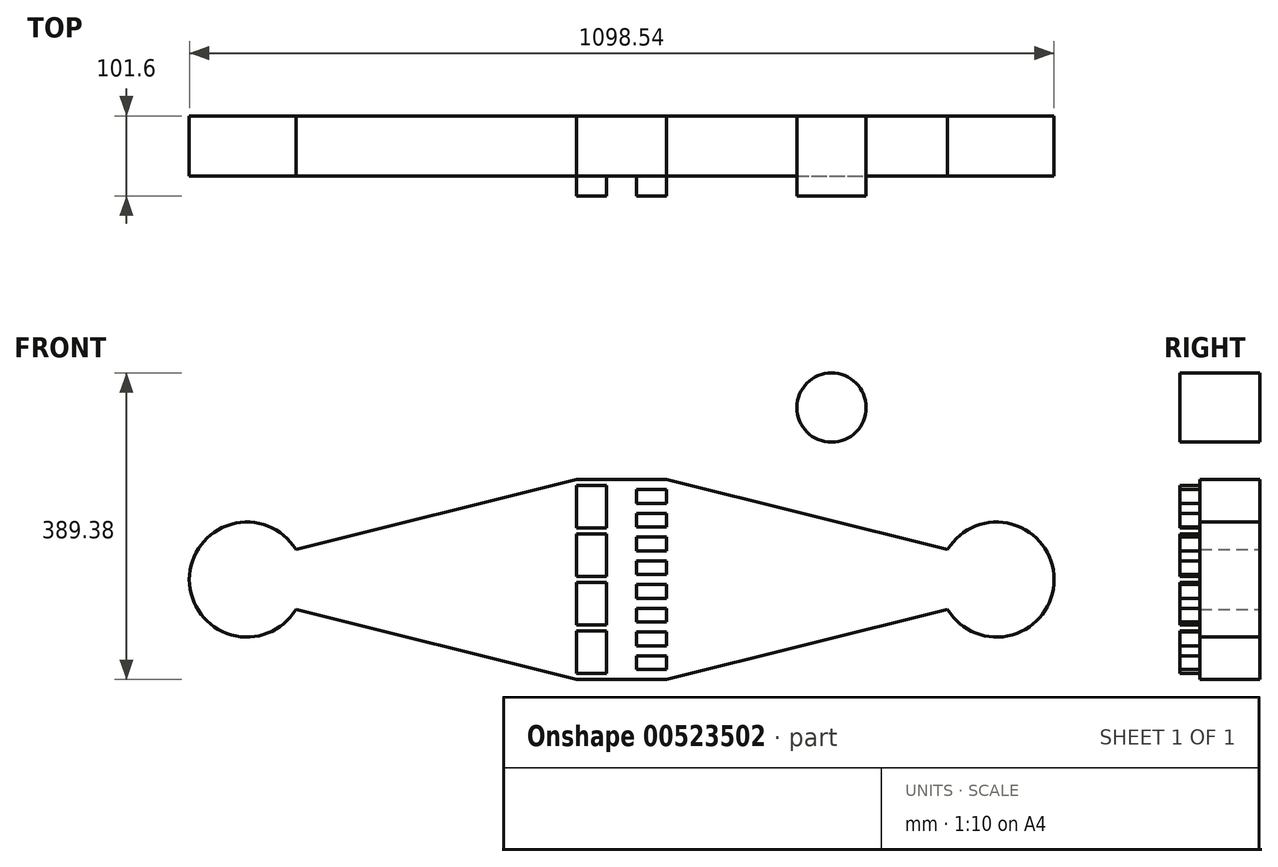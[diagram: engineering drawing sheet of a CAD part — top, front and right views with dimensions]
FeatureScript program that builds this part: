
annotation { "Feature Type Name" : "Feature", "Feature Type Description" : "" }
export const myFeature = defineFeature(function(context is Context, id is Id, definition is map)
    precondition{}
    {
        {
            var Q0;
            Q0=qCreatedBy(makeId("Front.planeOp"),FACE);
            var sketch = newSketch(context, id + "F0", { "sketchPlane" : qUnion([Q0])});
            skCircle(sketch, "E0", {"center": v(266.5, 218.44) * mm, "radius": 43.94 * mm});
            skCircle(sketch, "E1", {"center": v(266.5, -218.44) * mm, "radius": 43.94 * mm});
            skArc(sketch, "E2", {"start": v(-413.95, 38.1) * mm, "mid": v(-549.28, 0) * mm, "end": v(-413.95, -38.1) * mm});
            skArc(sketch, "E3", {"start": v(413.95, -38.1) * mm, "mid": v(549.28, 0) * mm, "end": v(413.95, 38.1) * mm});
            skLineSegment(sketch, "E4", {"start": v(-413.95, 38.1) * mm, "end": v(-57.53, 127) * mm});
            skLineSegment(sketch, "E5", {"start": v(-413.95, -38.1) * mm, "end": v(-57.53, -127) * mm});
            skLineSegment(sketch, "E6", {"start": v(56.77, 127) * mm, "end": v(413.95, 38.1) * mm});
            skLineSegment(sketch, "E7", {"start": v(56.77, -127) * mm, "end": v(413.95, -38.1) * mm});
            skLineSegment(sketch, "E8", {"start": v(-57.53, 127) * mm, "end": v(56.77, 127) * mm});
            skLineSegment(sketch, "E9", {"start": v(-57.53, -127) * mm, "end": v(56.77, -127) * mm});
            skCircle(sketch, "E10", {"center": v(-305.37, 218.44) * mm, "radius": 43.94 * mm});
            skCircle(sketch, "E11", {"center": v(-305.37, -218.44) * mm, "radius": 43.94 * mm});
            skLineSegment(sketch, "E12", {"start": v(-637.54, -320.04) * mm, "end": v(637.54, -320.04) * mm});
            skLineSegment(sketch, "E13", {"start": v(637.54, 320.04) * mm, "end": v(637.54, -320.04) * mm});
            skLineSegment(sketch, "E14", {"start": v(-637.54, 320.04) * mm, "end": v(-637.54, -320.04) * mm});
            skLineSegment(sketch, "E15", {"start": v(-57.53, 65.4) * mm, "end": v(-57.53, 119.38) * mm});
            skLineSegment(sketch, "E16", {"start": v(-57.53, 119.38) * mm, "end": v(-19.43, 119.38) * mm});
            skLineSegment(sketch, "E17", {"start": v(-19.43, 119.38) * mm, "end": v(-19.43, 65.4) * mm});
            skLineSegment(sketch, "E18", {"start": v(-19.43, 65.4) * mm, "end": v(-57.53, 65.4) * mm});
            skLineSegment(sketch, "E19", {"start": v(-57.53, 3.81) * mm, "end": v(-57.53, 57.79) * mm});
            skLineSegment(sketch, "E20", {"start": v(-57.53, 57.79) * mm, "end": v(-19.43, 57.79) * mm});
            skLineSegment(sketch, "E21", {"start": v(-19.43, 57.79) * mm, "end": v(-19.43, 3.81) * mm});
            skLineSegment(sketch, "E22", {"start": v(-19.43, 3.81) * mm, "end": v(-57.53, 3.81) * mm});
            skLineSegment(sketch, "E23", {"start": v(-57.53, -57.79) * mm, "end": v(-57.53, -3.81) * mm});
            skLineSegment(sketch, "E24", {"start": v(-57.53, -3.81) * mm, "end": v(-19.43, -3.81) * mm});
            skLineSegment(sketch, "E25", {"start": v(-19.43, -3.81) * mm, "end": v(-19.43, -57.79) * mm});
            skLineSegment(sketch, "E26", {"start": v(-19.43, -57.79) * mm, "end": v(-57.53, -57.79) * mm});
            skLineSegment(sketch, "E27", {"start": v(-57.53, -119.38) * mm, "end": v(-57.53, -65.4) * mm});
            skLineSegment(sketch, "E28", {"start": v(-57.53, -65.4) * mm, "end": v(-19.43, -65.4) * mm});
            skLineSegment(sketch, "E29", {"start": v(-19.43, -65.4) * mm, "end": v(-19.43, -119.38) * mm});
            skLineSegment(sketch, "E30", {"start": v(-19.43, -119.38) * mm, "end": v(-57.53, -119.38) * mm});
            skLineSegment(sketch, "E31", {"start": v(18.67, 96.84) * mm, "end": v(18.67, 114.3) * mm});
            skLineSegment(sketch, "E32", {"start": v(18.67, 114.3) * mm, "end": v(56.77, 114.3) * mm});
            skLineSegment(sketch, "E33", {"start": v(56.77, 114.3) * mm, "end": v(56.77, 96.84) * mm});
            skLineSegment(sketch, "E34", {"start": v(56.77, 96.84) * mm, "end": v(18.67, 96.84) * mm});
            skLineSegment(sketch, "E35", {"start": v(18.67, 66.68) * mm, "end": v(18.67, 84.14) * mm});
            skLineSegment(sketch, "E36", {"start": v(18.67, 84.14) * mm, "end": v(56.77, 84.14) * mm});
            skLineSegment(sketch, "E37", {"start": v(56.77, 84.14) * mm, "end": v(56.77, 66.68) * mm});
            skLineSegment(sketch, "E38", {"start": v(56.77, 66.68) * mm, "end": v(18.67, 66.68) * mm});
            skLineSegment(sketch, "E39", {"start": v(18.67, 36.51) * mm, "end": v(18.67, 53.98) * mm});
            skLineSegment(sketch, "E40", {"start": v(18.67, 53.98) * mm, "end": v(56.77, 53.98) * mm});
            skLineSegment(sketch, "E41", {"start": v(56.77, 53.98) * mm, "end": v(56.77, 36.51) * mm});
            skLineSegment(sketch, "E42", {"start": v(56.77, 36.51) * mm, "end": v(18.67, 36.51) * mm});
            skLineSegment(sketch, "E43", {"start": v(18.67, 6.35) * mm, "end": v(18.67, 23.81) * mm});
            skLineSegment(sketch, "E44", {"start": v(18.67, 23.81) * mm, "end": v(56.77, 23.81) * mm});
            skLineSegment(sketch, "E45", {"start": v(56.77, 23.81) * mm, "end": v(56.77, 6.35) * mm});
            skLineSegment(sketch, "E46", {"start": v(56.77, 6.35) * mm, "end": v(18.67, 6.35) * mm});
            skLineSegment(sketch, "E47", {"start": v(18.67, -23.81) * mm, "end": v(18.67, -6.35) * mm});
            skLineSegment(sketch, "E48", {"start": v(18.67, -6.35) * mm, "end": v(56.77, -6.35) * mm});
            skLineSegment(sketch, "E49", {"start": v(56.77, -6.35) * mm, "end": v(56.77, -23.81) * mm});
            skLineSegment(sketch, "E50", {"start": v(56.77, -23.81) * mm, "end": v(18.67, -23.81) * mm});
            skLineSegment(sketch, "E51", {"start": v(18.67, -53.98) * mm, "end": v(18.67, -36.51) * mm});
            skLineSegment(sketch, "E52", {"start": v(18.67, -36.51) * mm, "end": v(56.77, -36.51) * mm});
            skLineSegment(sketch, "E53", {"start": v(56.77, -36.51) * mm, "end": v(56.77, -53.98) * mm});
            skLineSegment(sketch, "E54", {"start": v(56.77, -53.98) * mm, "end": v(18.67, -53.98) * mm});
            skLineSegment(sketch, "E55", {"start": v(18.67, -84.14) * mm, "end": v(18.67, -66.68) * mm});
            skLineSegment(sketch, "E56", {"start": v(18.67, -66.68) * mm, "end": v(56.77, -66.68) * mm});
            skLineSegment(sketch, "E57", {"start": v(56.77, -66.68) * mm, "end": v(56.77, -84.14) * mm});
            skLineSegment(sketch, "E58", {"start": v(56.77, -84.14) * mm, "end": v(18.67, -84.14) * mm});
            skLineSegment(sketch, "E59", {"start": v(18.67, -114.3) * mm, "end": v(18.67, -96.84) * mm});
            skLineSegment(sketch, "E60", {"start": v(18.67, -96.84) * mm, "end": v(56.77, -96.84) * mm});
            skLineSegment(sketch, "E61", {"start": v(56.77, -96.84) * mm, "end": v(56.77, -114.3) * mm});
            skLineSegment(sketch, "E62", {"start": v(56.77, -114.3) * mm, "end": v(18.67, -114.3) * mm});
            skLineSegment(sketch, "E63", {"start": v(-637.54, 320.04) * mm, "end": v(637.54, 320.04) * mm});
            skLineSegment(sketch, "E64", {"start": v(637.54, -320.04) * mm, "end": v(-637.54, -320.04) * mm});
            skLineSegment(sketch, "E65", {"start": v(637.54, 320.04) * mm, "end": v(-637.54, 320.04) * mm});
            skSolve(sketch);
        }
        {
            var Q0;
            Q0=makeQuery(id+"F0.imprint","IMPRINT",FACE,{"disambiguationData":[TD([[makeQuery(id+"F0.imprint","IMPRINT",EDGE,{"derivedFrom":sQuery(id+"F0.wireOp",EDGE,"E0")}),1.0]])]});
            extrude(context, id + "F1", {"entities" : qUnion([Q0]), "depth" : 101.6 * mm, "offsetDistance" : 25.4 * mm});
        }
        {
            var Q0;
            Q0=makeQuery(id+"F0.imprint","IMPRINT",FACE,{"disambiguationData":[TD([[makeQuery(id+"F0.imprint","IMPRINT",EDGE,{"derivedFrom":sQuery(id+"F0.wireOp",EDGE,"E2")}),1.0]])]});
            extrude(context, id + "F2", {"entities" : qUnion([Q0]), "operationType" : NewBodyOperationType.ADD, "depth" : 76.2 * mm, "offsetDistance" : 25.4 * mm});
        }
        {
            var Q0;
            Q0=makeQuery(id+"F0.imprint","IMPRINT",FACE,{"disambiguationData":[TD([[makeQuery(id+"F0.imprint","IMPRINT",EDGE,{"derivedFrom":sQuery(id+"F0.wireOp",EDGE,"E19")}),-1.0]])]});
            var Q1;
            Q1=makeQuery(id+"F0.imprint","IMPRINT",FACE,{"disambiguationData":[TD([[makeQuery(id+"F0.imprint","IMPRINT",EDGE,{"derivedFrom":sQuery(id+"F0.wireOp",EDGE,"E23")}),-1.0]])]});
            var Q2;
            Q2=makeQuery(id+"F0.imprint","IMPRINT",FACE,{"disambiguationData":[TD([[makeQuery(id+"F0.imprint","IMPRINT",EDGE,{"derivedFrom":sQuery(id+"F0.wireOp",EDGE,"E27")}),-1.0]])]});
            var Q3;
            Q3=makeQuery(id+"F0.imprint","IMPRINT",FACE,{"disambiguationData":[TD([[makeQuery(id+"F0.imprint","IMPRINT",EDGE,{"derivedFrom":sQuery(id+"F0.wireOp",EDGE,"E59")}),-1.0]])]});
            var Q4;
            Q4=makeQuery(id+"F0.imprint","IMPRINT",FACE,{"disambiguationData":[TD([[makeQuery(id+"F0.imprint","IMPRINT",EDGE,{"derivedFrom":sQuery(id+"F0.wireOp",EDGE,"E55")}),-1.0]])]});
            var Q5;
            Q5=makeQuery(id+"F0.imprint","IMPRINT",FACE,{"disambiguationData":[TD([[makeQuery(id+"F0.imprint","IMPRINT",EDGE,{"derivedFrom":sQuery(id+"F0.wireOp",EDGE,"E51")}),-1.0]])]});
            var Q6;
            Q6=makeQuery(id+"F0.imprint","IMPRINT",FACE,{"disambiguationData":[TD([[makeQuery(id+"F0.imprint","IMPRINT",EDGE,{"derivedFrom":sQuery(id+"F0.wireOp",EDGE,"E47")}),-1.0]])]});
            var Q7;
            Q7=makeQuery(id+"F0.imprint","IMPRINT",FACE,{"disambiguationData":[TD([[makeQuery(id+"F0.imprint","IMPRINT",EDGE,{"derivedFrom":sQuery(id+"F0.wireOp",EDGE,"E39")}),-1.0]])]});
            var Q8;
            Q8=makeQuery(id+"F0.imprint","IMPRINT",FACE,{"disambiguationData":[TD([[makeQuery(id+"F0.imprint","IMPRINT",EDGE,{"derivedFrom":sQuery(id+"F0.wireOp",EDGE,"E31")}),-1.0]])]});
            var Q9;
            Q9=makeQuery(id+"F0.imprint","IMPRINT",FACE,{"disambiguationData":[TD([[makeQuery(id+"F0.imprint","IMPRINT",EDGE,{"derivedFrom":sQuery(id+"F0.wireOp",EDGE,"E35")}),-1.0]])]});
            var Q10;
            Q10=makeQuery(id+"F0.imprint","IMPRINT",FACE,{"disambiguationData":[TD([[makeQuery(id+"F0.imprint","IMPRINT",EDGE,{"derivedFrom":sQuery(id+"F0.wireOp",EDGE,"E43")}),-1.0]])]});
            var Q11;
            Q11=makeQuery(id+"F0.imprint","IMPRINT",FACE,{"disambiguationData":[TD([[makeQuery(id+"F0.imprint","IMPRINT",EDGE,{"derivedFrom":sQuery(id+"F0.wireOp",EDGE,"E15")}),-1.0]])]});
            extrude(context, id + "F3", {"entities" : qUnion([Q0, Q1, Q2, Q3, Q4, Q5, Q6, Q7, Q8, Q9, Q10, Q11]), "operationType" : NewBodyOperationType.ADD, "depth" : 101.6 * mm, "offsetDistance" : 25.4 * mm});
        }
    });
